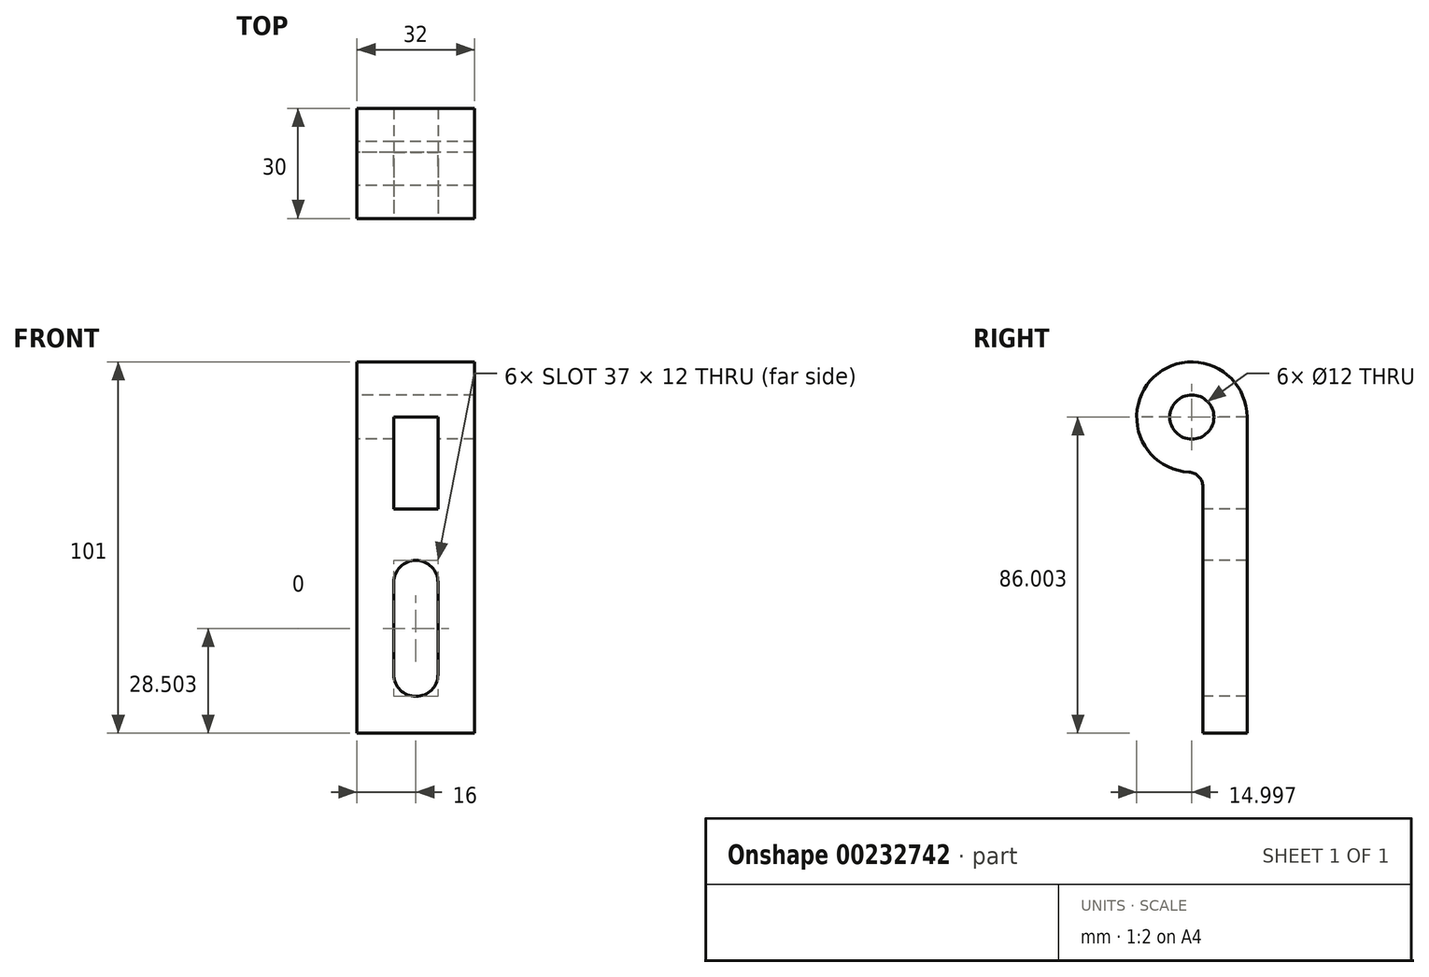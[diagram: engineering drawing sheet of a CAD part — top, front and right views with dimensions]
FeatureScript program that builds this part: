
annotation { "Feature Type Name" : "Feature", "Feature Type Description" : "" }
export const myFeature = defineFeature(function(context is Context, id is Id, definition is map)
    precondition{}
    {
        {
            var Q0;
            Q0=qCreatedBy(makeId("Right.planeOp"),FACE);
            var sketch = newSketch(context, id + "F0", { "sketchPlane" : qUnion([Q0])});
            skCircle(sketch, "E0", {"center": v(-8.54, 37.98) * mm, "radius": 6 * mm});
            skArc(sketch, "E1", {"start": v(6.46, 37.98) * mm, "mid": v(-18.87, 48.87) * mm, "end": v(-9.33, 23) * mm});
            skLineSegment(sketch, "E2", {"start": v(-5.54, 19) * mm, "end": v(-5.54, -48.02) * mm});
            skLineSegment(sketch, "E3", {"start": v(6.46, 37.98) * mm, "end": v(6.46, -48.02) * mm});
            skLineSegment(sketch, "E4", {"start": v(6.46, -48.02) * mm, "end": v(-5.54, -48.02) * mm});
            skPoint(sketch, "E5.visualSharp", {"position": v(-5.54, 23.29) * mm});
            skArc(sketch, "E5.filletArc", {"start": v(-5.54, 19) * mm, "mid": v(-6.64, 21.76) * mm, "end": v(-9.33, 23) * mm});
            skSolve(sketch);
        }
        {
            var Q0;
            Q0=makeQuery(id+"F0.imprint","IMPRINT",FACE,{"disambiguationData":[TD([[makeQuery(id+"F0.imprint","IMPRINT",EDGE,{"derivedFrom":sQuery(id+"F0.wireOp",EDGE,"E0")}),-1.0]])]});
            extrude(context, id + "F1", {"entities" : qUnion([Q0]), "depth" : 32 * mm});
        }
        {
            var Q0;
            Q0=qCreatedBy(makeId("Front.planeOp"),FACE);
            var sketch = newSketch(context, id + "F2", { "sketchPlane" : qUnion([Q0])});
            skLineSegment(sketch, "E6.0", {"start": v(32, 37.98) * mm, "end": v(32, -48.02) * mm});
            skLineSegment(sketch, "E7", {"start": v(0, 52.98) * mm, "end": v(32, 52.98) * mm});
            skLineSegment(sketch, "E8.0.0", {"start": v(0, -48.02) * mm, "end": v(0, 37.98) * mm});
            skLineSegment(sketch, "E8.0.1", {"start": v(0, 37.98) * mm, "end": v(32, 37.98) * mm});
            skLineSegment(sketch, "E8.0.3", {"start": v(32, -48.02) * mm, "end": v(0, -48.02) * mm});
            skLineSegment(sketch, "E9.0", {"start": v(32, 52.98) * mm, "end": v(32, 23) * mm});
            skLineSegment(sketch, "E10.0", {"start": v(0, 52.98) * mm, "end": v(0, 23) * mm});
            skLineSegment(sketch, "E11.bottom", {"start": v(22, 52.98) * mm, "end": v(10, 52.98) * mm});
            skLineSegment(sketch, "E11.top", {"start": v(22, 12.98) * mm, "end": v(10, 12.98) * mm});
            skLineSegment(sketch, "E11.left", {"start": v(22, 52.98) * mm, "end": v(22, 12.98) * mm});
            skLineSegment(sketch, "E11.right", {"start": v(10, 52.98) * mm, "end": v(10, 12.98) * mm});
            skArc(sketch, "E12", {"start": v(0, -32.02) * mm, "mid": v(16, -48.02) * mm, "end": v(32, -32.02) * mm});
            skPoint(sketch, "E12.centerSnap0", {"position": v(16, -48.02) * mm});
            skArc(sketch, "E13", {"start": v(10, -32.02) * mm, "mid": v(16, -38.02) * mm, "end": v(22, -32.02) * mm});
            skArc(sketch, "E14", {"start": v(22, -7.02) * mm, "mid": v(16, -1.02) * mm, "end": v(10, -7.02) * mm});
            skLineSegment(sketch, "E15", {"start": v(22, -7.02) * mm, "end": v(22, -32.02) * mm});
            skLineSegment(sketch, "E16", {"start": v(10, -7.02) * mm, "end": v(10, -32.02) * mm});
            skLineSegment(sketch, "E17", {"start": v(32, -32.02) * mm, "end": v(32, -48.02) * mm});
            skLineSegment(sketch, "E18", {"start": v(0, -48.02) * mm, "end": v(0, -32.02) * mm});
            skSolve(sketch);
        }
        {
            var Q0;
            {var subQ5=sQuery(id+"F2.wireOp",EDGE,"E11.top");Q0=makeQuery(id+"F2.imprint","IMPRINT",FACE,{"disambiguationData":[TD([[makeQuery(id+"F2.imprint","IMPRINT",EDGE,{"derivedFrom":subQ5}),-1.0]])]});}
            var Q1;
            {var subQ5=sQuery(id+"F2.wireOp",EDGE,"E11.bottom");Q1=makeQuery(id+"F2.imprint","IMPRINT",FACE,{"disambiguationData":[TD([[makeQuery(id+"F2.imprint","IMPRINT",EDGE,{"derivedFrom":subQ5}),1.0]])]});}
            var Q2;
            Q2=makeQuery(id+"F2.imprint","IMPRINT",FACE,{"disambiguationData":[TD([[makeQuery(id+"F2.imprint","IMPRINT",EDGE,{"derivedFrom":sQuery(id+"F2.wireOp",EDGE,"E13")}),1.0]])]});
            var Q3;
            {var subQ0=sQuery(id+"F2.wireOp",EDGE,"E17");Q3=makeQuery(id+"F2.imprint","IMPRINT",FACE,{"disambiguationData":[TD([[makeQuery(id+"F2.imprint","IMPRINT",EDGE,{"derivedFrom":subQ0}),-1.0]])]});}
            var Q4;
            {var subQ0=sQuery(id+"F2.wireOp",EDGE,"E18");Q4=makeQuery(id+"F2.imprint","IMPRINT",FACE,{"disambiguationData":[TD([[makeQuery(id+"F2.imprint","IMPRINT",EDGE,{"derivedFrom":subQ0}),-1.0]])]});}
            extrude(context, id + "F3", {"entities" : qUnion([Q0, Q1, Q2, Q3, Q4]), "operationType" : NewBodyOperationType.REMOVE, "endBound" : BoundingType.SYMMETRIC, "oppositeDirection" : true, "depth" : 66.6 * mm});
        }
    });
